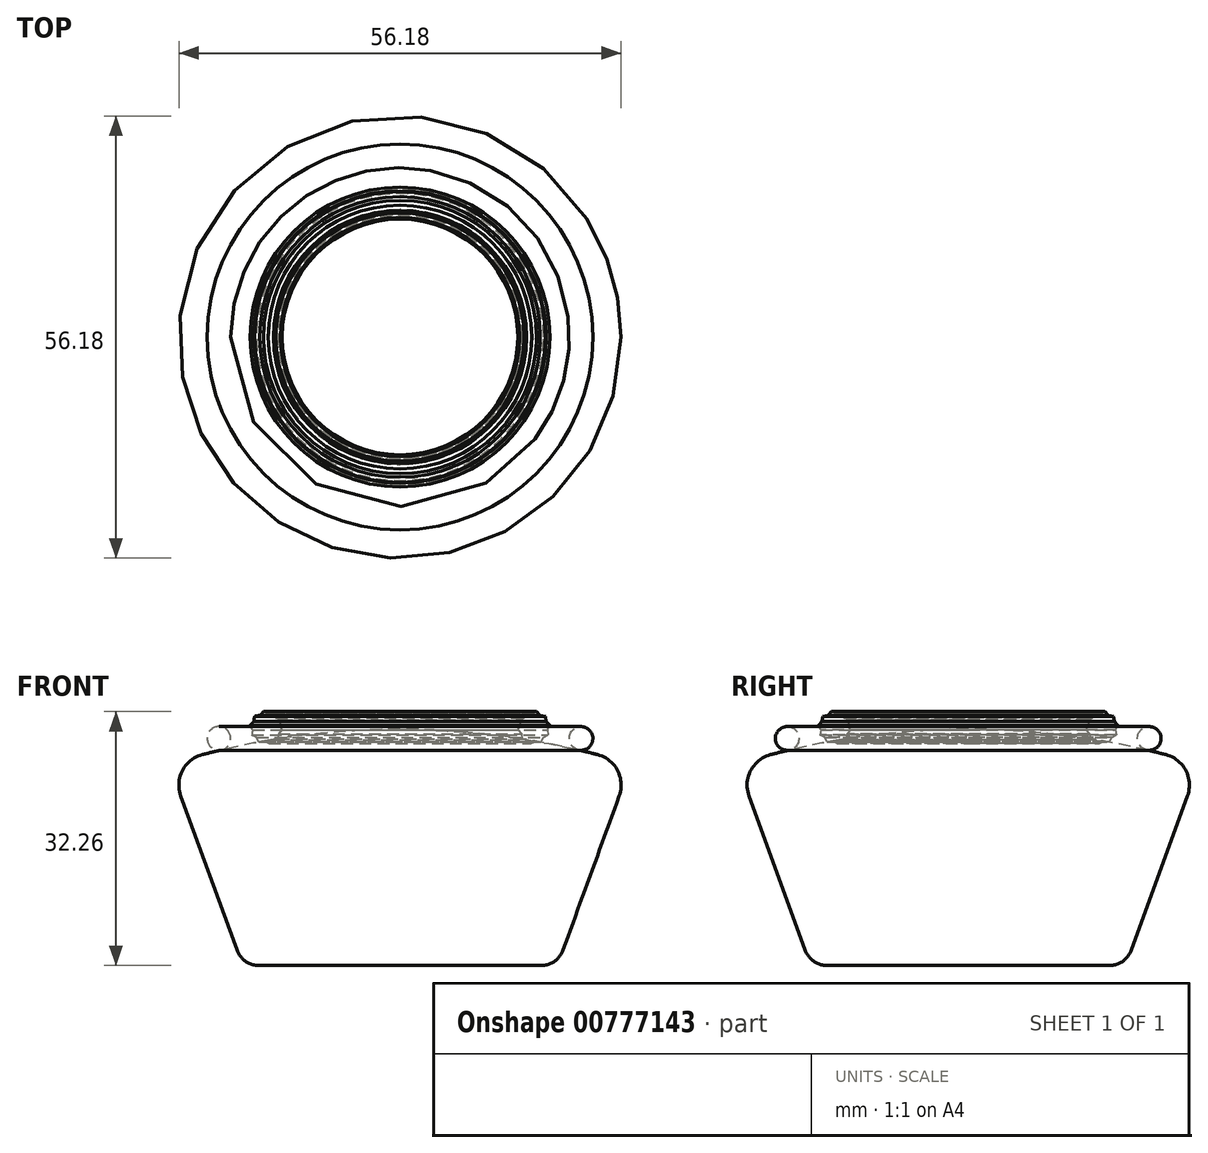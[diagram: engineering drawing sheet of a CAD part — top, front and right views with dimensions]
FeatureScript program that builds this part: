
annotation { "Feature Type Name" : "Feature", "Feature Type Description" : "" }
export const myFeature = defineFeature(function(context is Context, id is Id, definition is map)
    precondition{}
    {
        {
            var Q0;
            Q0=qCreatedBy(makeId("Front.planeOp"),FACE);
            var sketch = newSketch(context, id + "F0", { "sketchPlane" : qUnion([Q0])});
            skLineSegment(sketch, "E0", {"start": v(29.32, 25.6) * mm, "end": v(20, 0) * mm});
            skLineSegment(sketch, "E1", {"start": v(20, 0) * mm, "end": v(0, 0) * mm});
            skLineSegment(sketch, "E2", {"start": v(0, 0) * mm, "end": v(0, 30) * mm});
            skArc(sketch, "E3", {"start": v(29.32, 25.6) * mm, "mid": v(14.82, 28.9) * mm, "end": v(0, 30) * mm});
            skSolve(sketch);
        }
        {
            var Q0;
            Q0=makeQuery(id+"F0.imprint","IMPRINT",FACE,{"disambiguationData":[TD([[makeQuery(id+"F0.imprint","IMPRINT",EDGE,{"derivedFrom":sQuery(id+"F0.wireOp",EDGE,"E0")}),-1.0]])]});
            var Q1;
            Q1=sQuery(id+"F0.wireOp",EDGE,"E2");
            revolve(context, id + "F1", {"surfaceOperationType" : NewSurfaceOperationType.NEW, "entities" : qUnion([Q0]), "axis" : qUnion([Q1]), "revolveType" : RevolveType.FULL});
        }
        {
            var Q0;
            Q0=makeQuery(id+"F1.opRevolve","SWEPT_EDGE",EDGE,{"disambiguationData":[OSD([sQuery(id+"F0.wireOp",EDGE,"E0"),sQuery(id+"F0.wireOp",EDGE,"E1")])]});
            fillet(context, id + "F2", {"entities" : qUnion([Q0]), "radius" : 3 * mm, "tangentPropagation" : true, "allowEdgeOverflow" : false});
        }
        {
            var Q0;
            Q0=makeQuery(id+"F1.opRevolve","SWEPT_EDGE",EDGE,{"disambiguationData":[OSD([sQuery(id+"F0.wireOp",EDGE,"E0"),sQuery(id+"F0.wireOp",EDGE,"E3")])]});
            fillet(context, id + "F3", {"entities" : qUnion([Q0]), "radius" : 4 * mm, "tangentPropagation" : true, "allowEdgeOverflow" : false});
        }
        {
            var Q0;
            Q0=qCreatedBy(makeId("Front.planeOp"),FACE);
            var sketch = newSketch(context, id + "F4", { "sketchPlane" : qUnion([Q0])});
            skCircle(sketch, "E4", {"center": v(23, 28.86) * mm, "radius": 1.5 * mm});
            skCircle(sketch, "E5.cCircle", {"center": v(17, 30.23) * mm, "radius": 1.66 * mm, "construction": true});
            skLineSegment(sketch, "E5.0", {"start": v(17.34, 32.26) * mm, "end": v(17.81, 31.78) * mm});
            skLineSegment(sketch, "E5.1", {"start": v(19.04, 30.53) * mm, "end": v(18.73, 29.94) * mm});
            skLineSegment(sketch, "E5.2", {"start": v(17.91, 28.39) * mm, "end": v(17.25, 28.5) * mm});
            skLineSegment(sketch, "E5.3", {"start": v(15.53, 28.8) * mm, "end": v(15.43, 29.46) * mm});
            skLineSegment(sketch, "E5.4", {"start": v(15.18, 31.19) * mm, "end": v(15.78, 31.48) * mm});
            skPoint(sketch, "E5.0.midPoint", {"position": v(18.19, 31.4) * mm});
            skLineSegment(sketch, "E6.0", {"start": v(16.09, 32.08) * mm, "end": v(16.75, 31.96) * mm});
            skLineSegment(sketch, "E6.1", {"start": v(18.47, 31.67) * mm, "end": v(18.57, 31.01) * mm});
            skLineSegment(sketch, "E6.2", {"start": v(18.82, 29.28) * mm, "end": v(18.22, 28.98) * mm});
            skLineSegment(sketch, "E6.3", {"start": v(16.66, 28.2) * mm, "end": v(16.19, 28.68) * mm});
            skLineSegment(sketch, "E6.4", {"start": v(14.96, 29.93) * mm, "end": v(15.27, 30.53) * mm});
            skPoint(sketch, "E6.0.midPoint", {"position": v(17.28, 31.87) * mm});
            skLineSegment(sketch, "E7", {"start": v(17, 30.23) * mm, "end": v(16.26, 31.72) * mm});
            skLineSegment(sketch, "E8.trimOffspring", {"start": v(16.75, 31.96) * mm, "end": v(17.34, 32.26) * mm});
            skLineSegment(sketch, "E9.trimOffspring", {"start": v(17.81, 31.78) * mm, "end": v(18.47, 31.67) * mm});
            skLineSegment(sketch, "E10.trimOffspring", {"start": v(18.57, 31.01) * mm, "end": v(19.04, 30.53) * mm});
            skLineSegment(sketch, "E11.trimOffspring", {"start": v(18.73, 29.94) * mm, "end": v(18.82, 29.28) * mm});
            skLineSegment(sketch, "E12.trimOffspring", {"start": v(18.22, 28.98) * mm, "end": v(17.91, 28.39) * mm});
            skLineSegment(sketch, "E13.trimOffspring", {"start": v(17.25, 28.5) * mm, "end": v(16.66, 28.2) * mm});
            skLineSegment(sketch, "E14.trimOffspring", {"start": v(16.19, 28.68) * mm, "end": v(15.53, 28.8) * mm});
            skLineSegment(sketch, "E15.trimOffspring", {"start": v(15.43, 29.46) * mm, "end": v(14.96, 29.93) * mm});
            skLineSegment(sketch, "E16.trimOffspring", {"start": v(15.27, 30.53) * mm, "end": v(15.18, 31.19) * mm});
            skLineSegment(sketch, "E17.trimOffspring", {"start": v(15.78, 31.48) * mm, "end": v(16.09, 32.08) * mm});
            skSolve(sketch);
        }
        {
            var Q0;
            Q0=makeQuery(id+"F4.imprint","IMPRINT",FACE,{"disambiguationData":[TD([[makeQuery(id+"F4.imprint","IMPRINT",EDGE,{"derivedFrom":sQuery(id+"F4.wireOp",EDGE,"E4")}),1.0]])]});
            var Q1;
            Q1=sQuery(id+"F0.wireOp",EDGE,"E2");
            revolve(context, id + "F5", {"operationType" : NewBodyOperationType.ADD, "surfaceOperationType" : NewSurfaceOperationType.NEW, "entities" : qUnion([Q0]), "axis" : qUnion([Q1]), "revolveType" : RevolveType.FULL});
        }
        {
            var Q0;
            Q0=makeQuery(id+"F4.imprint","IMPRINT",FACE,{"disambiguationData":[TD([[makeQuery(id+"F4.imprint","IMPRINT",EDGE,{"derivedFrom":sQuery(id+"F4.wireOp",EDGE,"E5.0")}),-1.0]])]});
            var Q1;
            Q1=sQuery(id+"F0.wireOp",EDGE,"E2");
            revolve(context, id + "F6", {"surfaceOperationType" : NewSurfaceOperationType.NEW, "entities" : qUnion([Q0]), "axis" : qUnion([Q1]), "revolveType" : RevolveType.FULL});
        }
    });
